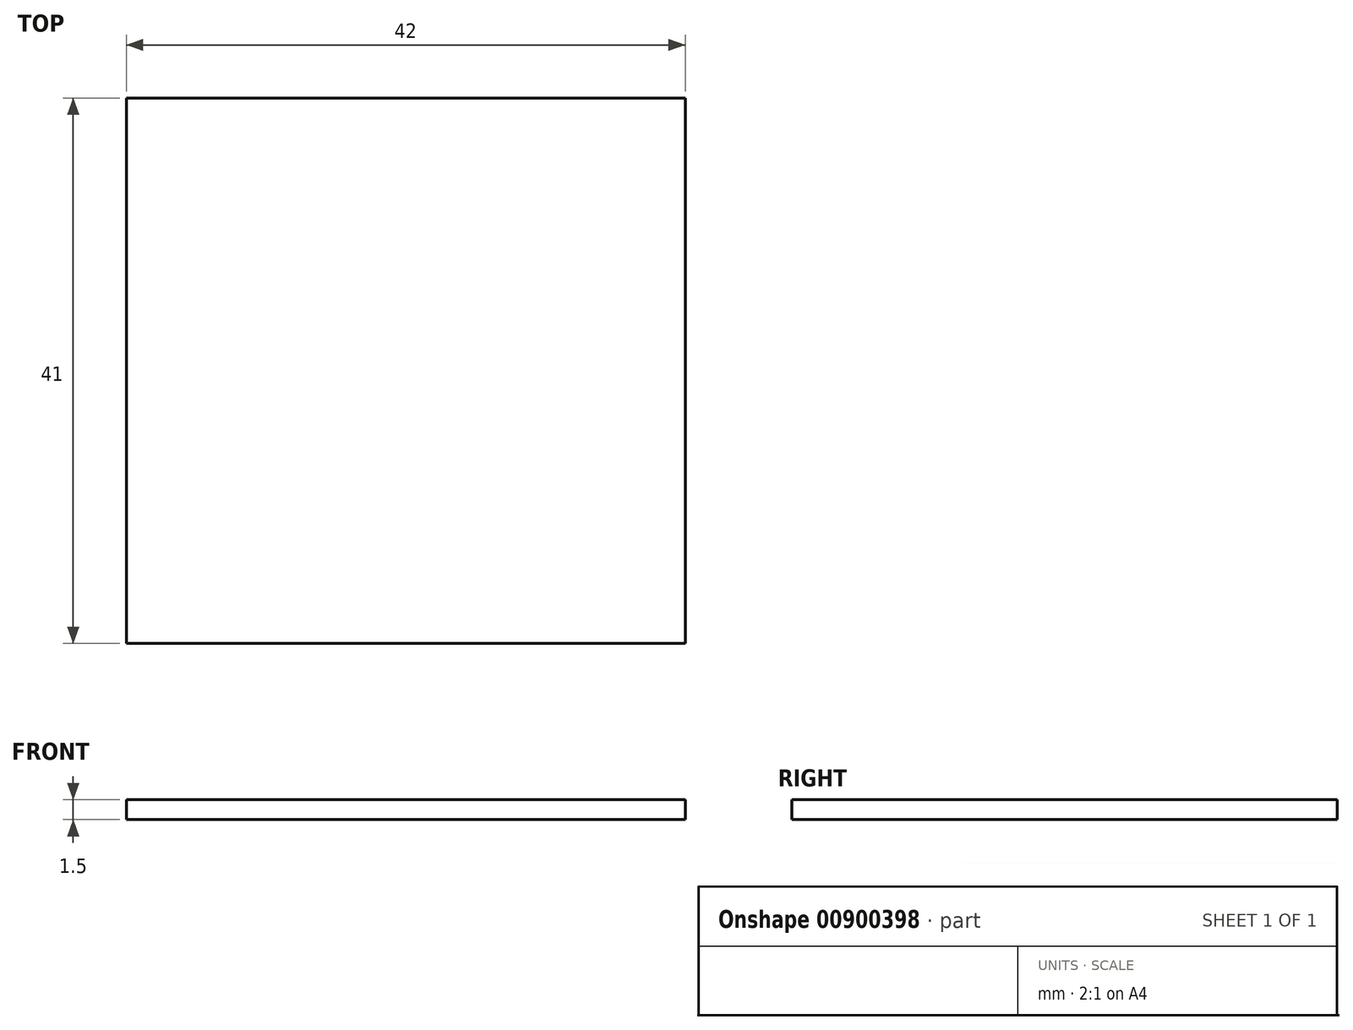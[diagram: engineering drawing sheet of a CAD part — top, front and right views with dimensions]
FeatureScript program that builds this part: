
annotation { "Feature Type Name" : "Feature", "Feature Type Description" : "" }
export const myFeature = defineFeature(function(context is Context, id is Id, definition is map)
    precondition{}
    {
        {
            var Q0;
            Q0=qCreatedBy(makeId("Top.planeOp"),FACE);
            var sketch = newSketch(context, id + "F0", { "sketchPlane" : qUnion([Q0])});
            skLineSegment(sketch, "E0.bottom", {"start": v(21, -20.5) * mm, "end": v(-21, -20.5) * mm});
            skLineSegment(sketch, "E0.top", {"start": v(21, 20.5) * mm, "end": v(-21, 20.5) * mm});
            skLineSegment(sketch, "E0.left", {"start": v(21, -20.5) * mm, "end": v(21, 20.5) * mm});
            skLineSegment(sketch, "E0.right", {"start": v(-21, -20.5) * mm, "end": v(-21, 20.5) * mm});
            skPoint(sketch, "E0.middle", {"position": v(0, 0) * mm});
            skLineSegment(sketch, "E1.bottom", {"start": v(21, -20.5) * mm, "end": v(13.5, -20.5) * mm});
            skLineSegment(sketch, "E1.left", {"start": v(21, -20.5) * mm, "end": v(21, -11.5) * mm});
            skSolve(sketch);
        }
        {
            var Q0;
            Q0=makeQuery(id+"F0.imprint","IMPRINT",FACE,{"disambiguationData":[TD([[makeQuery(id+"F0.imprint","IMPRINT",EDGE,{"derivedFrom":sQuery(id+"F0.wireOp",EDGE,"E0.bottom")}),-1.0]])]});
            extrude(context, id + "F1", {"entities" : qUnion([Q0]), "depth" : 1.5 * mm, "offsetDistance" : 25 * mm});
        }
    });
